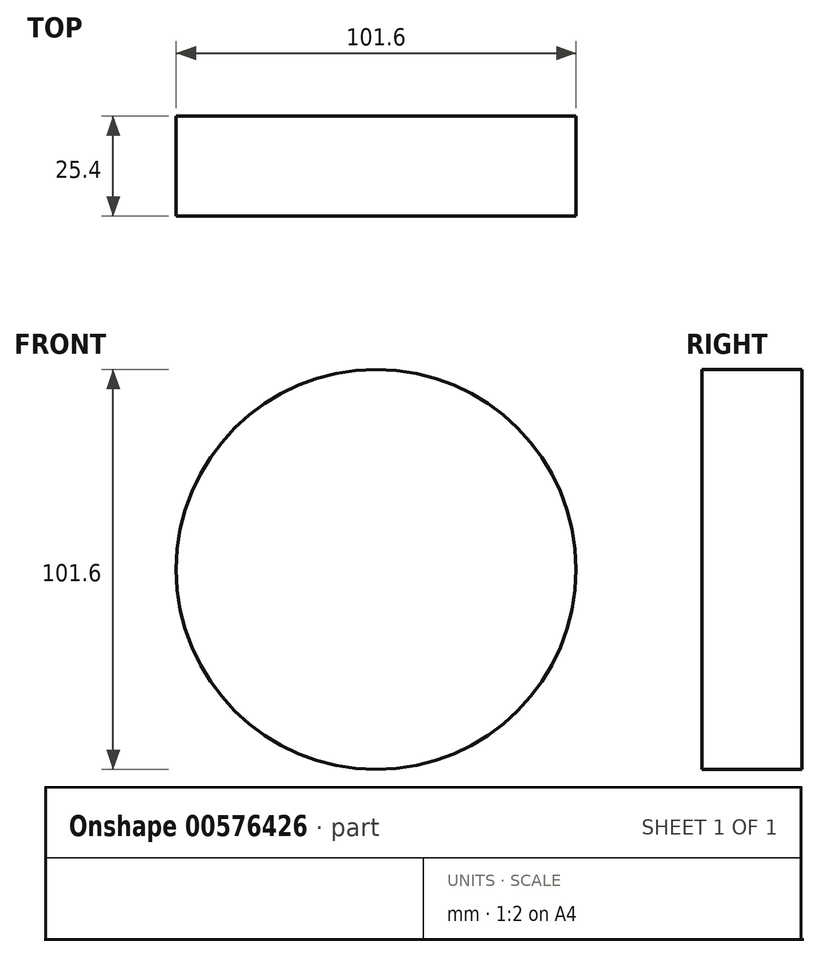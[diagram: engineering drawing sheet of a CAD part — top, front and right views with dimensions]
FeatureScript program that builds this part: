
annotation { "Feature Type Name" : "Feature", "Feature Type Description" : "" }
export const myFeature = defineFeature(function(context is Context, id is Id, definition is map)
    precondition{}
    {
        {
            var Q0;
            Q0=qCreatedBy(makeId("Front.planeOp"),FACE);
            var sketch = newSketch(context, id + "F0", { "sketchPlane" : qUnion([Q0])});
            skCircle(sketch, "E0", {"center": v(0, 0) * mm, "radius": 50.8 * mm});
            skLineSegment(sketch, "E1", {"start": v(-56.9, -12.73) * mm, "end": v(-56.9, -76.23) * mm});
            skLineSegment(sketch, "E2", {"start": v(-97.53, -12.73) * mm, "end": v(-97.53, -76.23) * mm});
            skArc(sketch, "E3", {"start": v(-97.53, -12.73) * mm, "mid": v(-77.21, 7.59) * mm, "end": v(-56.9, -12.73) * mm});
            skArc(sketch, "E4", {"start": v(-97.53, -76.23) * mm, "mid": v(-77.21, -96.55) * mm, "end": v(-56.9, -76.23) * mm});
            skLineSegment(sketch, "E5", {"start": v(-97.53, -12.73) * mm, "end": v(-56.9, -12.73) * mm, "construction": true});
            skLineSegment(sketch, "E6", {"start": v(-97.53, -76.23) * mm, "end": v(-56.9, -76.23) * mm, "construction": true});
            skLineSegment(sketch, "E7", {"start": v(-77.21, 7.59) * mm, "end": v(-77.21, -96.55) * mm, "construction": true});
            skSolve(sketch);
        }
        {
            var Q0;
            Q0=sQuery(id+"F0.wireOp",EDGE,"E0");
            extrude(context, id + "F1", {"bodyType" : ToolBodyType.SURFACE, "surfaceEntities" : qUnion([Q0]), "endBound" : BoundingType.SYMMETRIC, "depth" : 25.4 * mm, "offsetDistance" : 25.4 * mm});
        }
    });
